# Revit family: Baluster_Tapered
name_source: partatom
category: Balusters
units: mm (PartAtom-declared; Revit-internal decimal feet)

## family parameters
Always vertical = Yes
Classification Number = 23.30.70.21.11.14
Cut with Voids When Loaded = No
Shared = No

## types (2) — shared parameters
Assembly Code = C2020300
Construction Details = http://www.arcat.com
Description = Baluster
Green Building-LEED = http://www.arcat.com
Keynote = 06440
Lower Pin = 0' - 0 1/4"
Lower Turning Radius = 0' - 0 1/4"
Manufacturer = Generic
Manufacturer Fax = (203) 939-2444
Manufacturer Website = http://www.arcat.com
Model = Generic
Post = No
Product Data = http://www.arcat.com
Product Properties = http://www.arcat.com
Specification = http://www.arcat.com
StartPnt = 0' - 0 1/4"
Taper Start - Lower = 0' - 6"
Taper Start - Upper = 0' - 1"
Upper Turning Radius = 0' - 0 3/8"

## per-type parameters (varying)
| type | Baluster Material | MxWdth | Width |
| 1" | Wood - Cherry | 0' - 3" | 0' - 1" |
| 1 1/2" | Wood - Pressure Treated | 0' - 3 1/2" | 0' - 1 1/2" |
